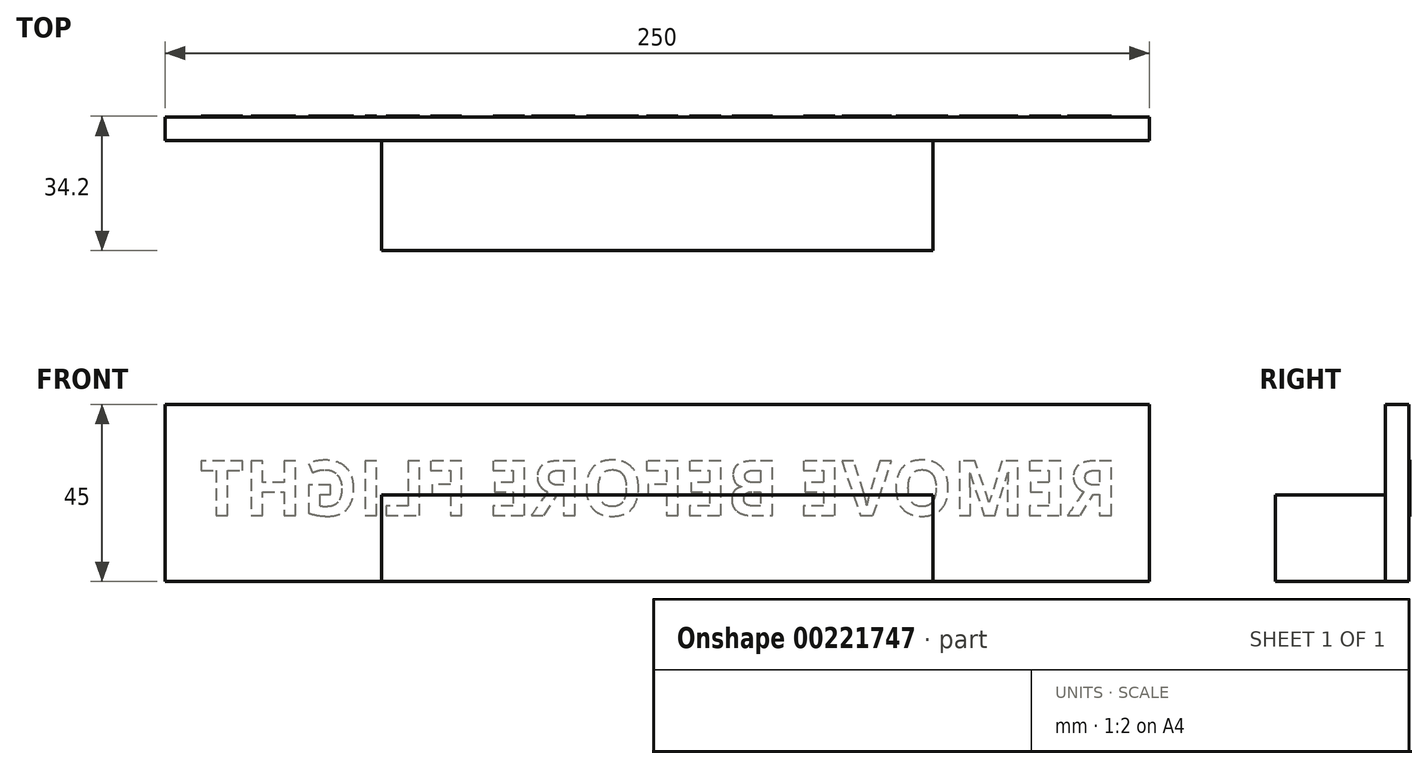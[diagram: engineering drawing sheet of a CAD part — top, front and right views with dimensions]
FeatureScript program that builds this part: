
annotation { "Feature Type Name" : "Feature", "Feature Type Description" : "" }
export const myFeature = defineFeature(function(context is Context, id is Id, definition is map)
    precondition{}
    {
        {
            var Q0;
            Q0=qCreatedBy(makeId("Front.planeOp"),FACE);
            var sketch = newSketch(context, id + "F0", { "sketchPlane" : qUnion([Q0])});
            skLineSegment(sketch, "E0.bottom", {"start": v(-125, 22.5) * mm, "end": v(125, 22.5) * mm});
            skLineSegment(sketch, "E0.top", {"start": v(-125, -22.5) * mm, "end": v(125, -22.5) * mm});
            skLineSegment(sketch, "E0.left", {"start": v(-125, 22.5) * mm, "end": v(-125, -22.5) * mm});
            skLineSegment(sketch, "E0.right", {"start": v(125, 22.5) * mm, "end": v(125, -22.5) * mm});
            skPoint(sketch, "E0.middle", {"position": v(0, 0) * mm});
            skSolve(sketch);
        }
        {
            var Q0;
            Q0 = qSketchRegion(id + "F0", true);
            extrude(context, id + "F1", {"entities" : qUnion([Q0]), "depth" : 6 * mm});
        }
        {
            var Q0;
            Q0=makeQuery(id+"F1.opExtrude","CAP_FACE",FACE,{"disambiguationData":[OSD([sQuery(id+"F0.wireOp",EDGE,"E0.bottom"),sQuery(id+"F0.wireOp",EDGE,"E0.top"),sQuery(id+"F0.wireOp",EDGE,"E0.left"),sQuery(id+"F0.wireOp",EDGE,"E0.right")])],"isStart":false});
            var sketch = newSketch(context, id + "F2", { "sketchPlane" : qUnion([Q0])});
            skLineSegment(sketch, "E1.0", {"start": v(-125, -22.5) * mm, "end": v(125, -22.5) * mm});
            skLineSegment(sketch, "E2", {"start": v(-70, -22.5) * mm, "end": v(-70, -0.5) * mm});
            skLineSegment(sketch, "E3", {"start": v(-70, -0.5) * mm, "end": v(70, -0.5) * mm});
            skLineSegment(sketch, "E4", {"start": v(70, -0.5) * mm, "end": v(70, -22.5) * mm});
            skSolve(sketch);
        }
        {
            var Q0;
            Q0 = qSketchRegion(id + "F2", true);
            extrude(context, id + "F3", {"entities" : qUnion([Q0]), "operationType" : NewBodyOperationType.ADD, "depth" : 28 * mm});
        }
        {
            var Q0;
            Q0=makeQuery(id+"F1.opExtrude","CAP_FACE",FACE,{"disambiguationData":[OSD([sQuery(id+"F0.wireOp",EDGE,"E0.bottom"),sQuery(id+"F0.wireOp",EDGE,"E0.top"),sQuery(id+"F0.wireOp",EDGE,"E0.left"),sQuery(id+"F0.wireOp",EDGE,"E0.right")])],"isStart":true});
            var sketch = newSketch(context, id + "F4", { "sketchPlane" : qUnion([Q0])});
            skText(sketch, "E5", { "text": "REMOVE BEFORE FLIGHT", "fontName": "OpenSans-Bold.ttf"});
            const initialGuessF4  = {"E5": [-0.11709, -0.00577, 1, 0, 0.014]};
            skSetInitialGuess(sketch, initialGuessF4);
            skSolve(sketch);
        }
        {
            var Q0;
            Q0 = qSketchRegion(id + "F4", true);
            extrude(context, id + "F5", {"entities" : qUnion([Q0]), "operationType" : NewBodyOperationType.ADD, "depth" : .2 * mm});
        }
    });
